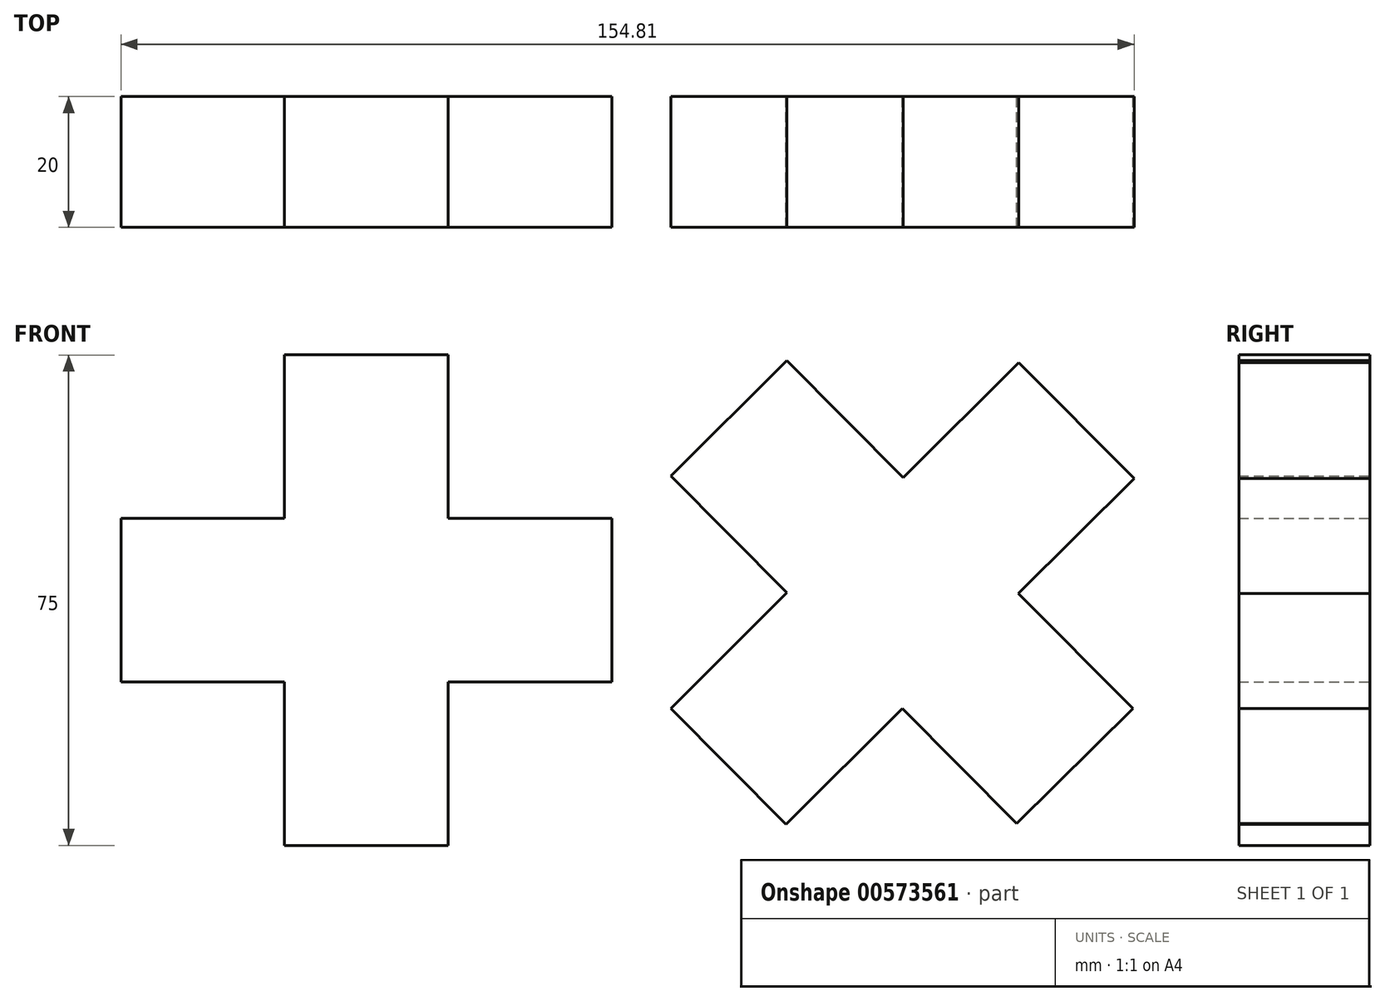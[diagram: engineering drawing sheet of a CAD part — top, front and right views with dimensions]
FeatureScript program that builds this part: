
annotation { "Feature Type Name" : "Feature", "Feature Type Description" : "" }
export const myFeature = defineFeature(function(context is Context, id is Id, definition is map)
    precondition{}
    {
        {
            var Q0;
            Q0=qCreatedBy(makeId("Front.planeOp"),FACE);
            var sketch = newSketch(context, id + "F0", { "sketchPlane" : qUnion([Q0])});
            skLineSegment(sketch, "E0.bottom", {"start": v(-75, 9.87) * mm, "end": v(0, 9.87) * mm});
            skLineSegment(sketch, "E0.top", {"start": v(-75, -15.13) * mm, "end": v(0, -15.13) * mm});
            skLineSegment(sketch, "E0.left", {"start": v(-75, 9.87) * mm, "end": v(-75, -15.13) * mm});
            skLineSegment(sketch, "E0.right", {"start": v(0, 9.87) * mm, "end": v(0, -15.13) * mm});
            skSolve(sketch);
        }
        {
            var Q0;
            Q0=qCreatedBy(makeId("Front.planeOp"),FACE);
            var sketch = newSketch(context, id + "F1", { "sketchPlane" : qUnion([Q0])});
            skLineSegment(sketch, "E1.bottom", {"start": v(-25, 34.87) * mm, "end": v(-25, -40.13) * mm});
            skLineSegment(sketch, "E1.top", {"start": v(-50, 34.87) * mm, "end": v(-50, -40.13) * mm});
            skLineSegment(sketch, "E1.left", {"start": v(-25, 34.87) * mm, "end": v(-50, 34.87) * mm});
            skLineSegment(sketch, "E1.right", {"start": v(-25, -40.13) * mm, "end": v(-50, -40.13) * mm});
            skSolve(sketch);
        }
        {
            var Q0;
            Q0=qCreatedBy(makeId("Front.planeOp"),FACE);
            var sketch = newSketch(context, id + "F2", { "sketchPlane" : qUnion([Q0])});
            skLineSegment(sketch, "E2.bottom", {"start": v(26.73, 34) * mm, "end": v(79.61, -19.17) * mm});
            skLineSegment(sketch, "E2.top", {"start": v(9, 16.38) * mm, "end": v(61.89, -36.8) * mm});
            skLineSegment(sketch, "E2.left", {"start": v(26.73, 34) * mm, "end": v(9, 16.38) * mm});
            skLineSegment(sketch, "E2.right", {"start": v(79.61, -19.17) * mm, "end": v(61.89, -36.8) * mm});
            skLineSegment(sketch, "E3.bottom", {"start": v(79.8, 15.99) * mm, "end": v(26.63, -36.9) * mm});
            skLineSegment(sketch, "E3.top", {"start": v(62.18, 33.71) * mm, "end": v(9, -19.17) * mm});
            skLineSegment(sketch, "E3.left", {"start": v(79.8, 15.99) * mm, "end": v(62.18, 33.71) * mm});
            skLineSegment(sketch, "E3.right", {"start": v(26.63, -36.9) * mm, "end": v(9, -19.17) * mm});
            skSolve(sketch);
        }
        {
            var Q0;
            Q0 = qSketchRegion(id + "F0", true);
            extrude(context, id + "F3", {"entities" : qUnion([Q0]), "depth" : 20 * mm, "offsetDistance" : 25 * mm});
        }
        {
            var Q0;
            Q0 = qSketchRegion(id + "F1", true);
            extrude(context, id + "F4", {"entities" : qUnion([Q0]), "operationType" : NewBodyOperationType.ADD, "depth" : 20 * mm, "offsetDistance" : 25 * mm});
        }
        {
            var Q0;
            Q0 = qSketchRegion(id + "F2", true);
            extrude(context, id + "F5", {"entities" : qUnion([Q0]), "depth" : 20 * mm, "offsetDistance" : 25 * mm});
        }
    });
